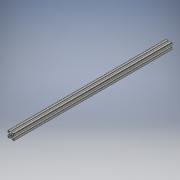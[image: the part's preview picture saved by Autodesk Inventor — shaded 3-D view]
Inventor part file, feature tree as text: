
AUTODESK INVENTOR PART (.ipt)
format: ipt  version: 2016 (Build 200138000, 138)  size: 1,068,032 bytes
history: native  units: in
note: dims shown in document units (in); Inventor stores cm internally (conversion verified against a paired STEP export)
features: extrude x1, sketch x1
ambient origin geometry x8: Origin, YZ Plane, XZ Plane, XY Plane, X Axis, Y Axis, Z Axis, Center Point
bodies: Solid1 (feature_tree)
feature tree (2):
  extrude  "Extrusion1"  [1 undecoded]
  sketch  "Sketch1"  dims[d0=29.5276in d1=0.0in]
note: 1 required parameter value undecoded (feature->parameter linkage not recoverable at this tier; creation-order binding heuristic only, values carry confidence <= 0.55)
